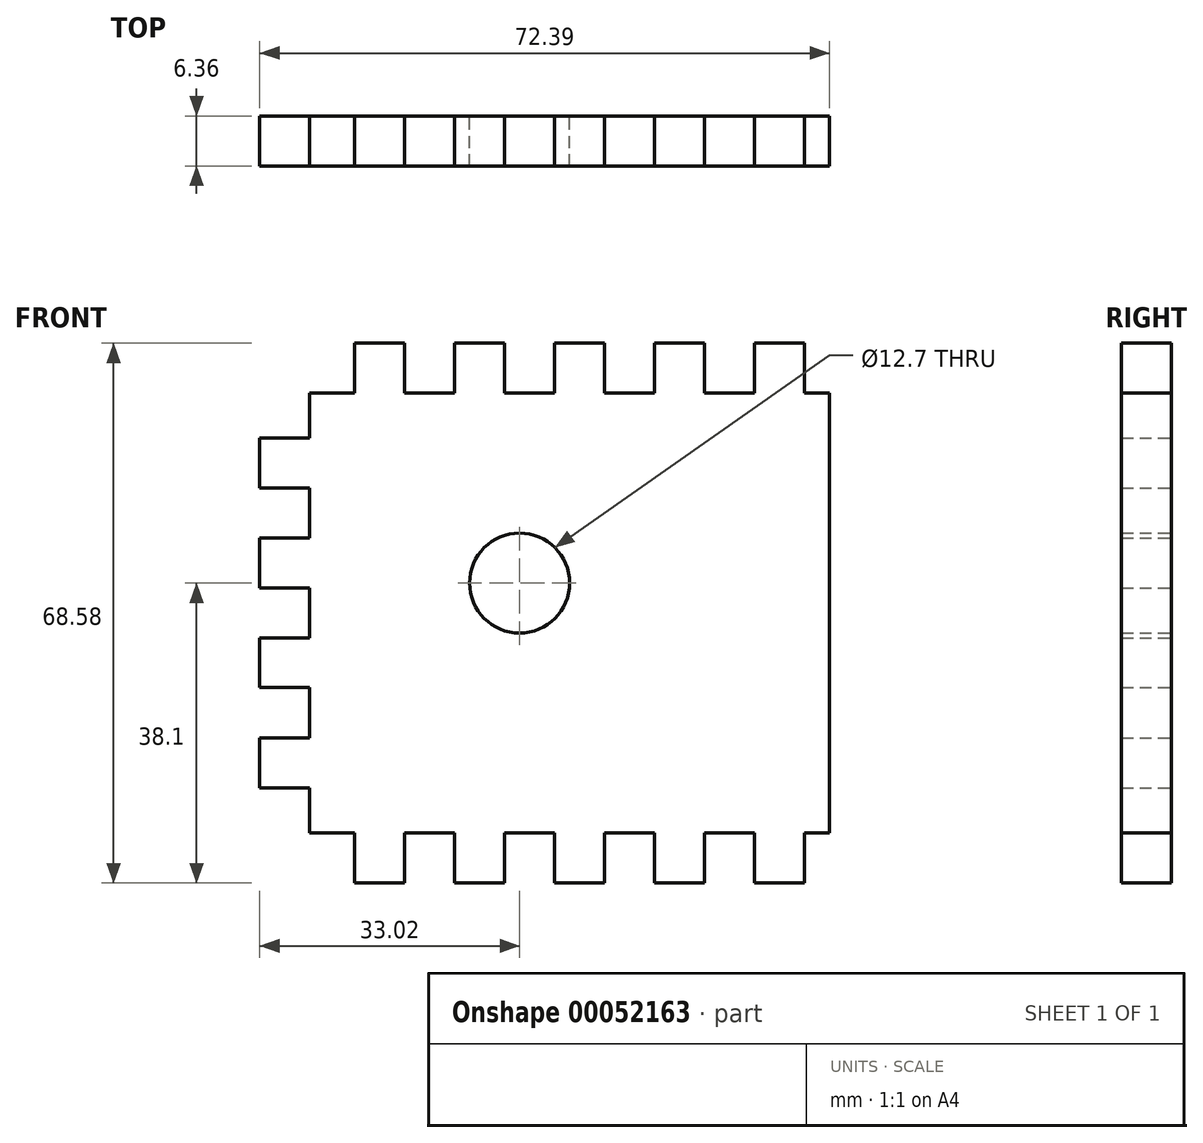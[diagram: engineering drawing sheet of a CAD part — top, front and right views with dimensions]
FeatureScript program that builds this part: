
annotation { "Feature Type Name" : "Feature", "Feature Type Description" : "" }
export const myFeature = defineFeature(function(context is Context, id is Id, definition is map)
    precondition{}
    {
        {
            var Q0;
            Q0=qCreatedBy(makeId("Front.planeOp"),FACE);
            var sketch = newSketch(context, id + "F0", { "sketchPlane" : qUnion([Q0])});
            skLineSegment(sketch, "E0.rect.bottom", {"start": v(33.02, 27.94) * mm, "end": v(29.85, 27.94) * mm});
            skLineSegment(sketch, "E0.rect.top", {"start": v(33.02, -27.94) * mm, "end": v(29.85, -27.94) * mm});
            skLineSegment(sketch, "E0.rect.left", {"start": v(33.02, 27.94) * mm, "end": v(33.02, -27.94) * mm});
            skPoint(sketch, "E0.rect.middle", {"position": v(0, 0) * mm});
            skLineSegment(sketch, "E1.top", {"start": v(23.5, 34.3) * mm, "end": v(29.85, 34.3) * mm});
            skLineSegment(sketch, "E1.left", {"start": v(23.5, 27.94) * mm, "end": v(23.5, 34.3) * mm});
            skLineSegment(sketch, "E1.right", {"start": v(29.85, 27.94) * mm, "end": v(29.85, 34.3) * mm});
            skLineSegment(sketch, "E2.1.0.1", {"start": v(10.8, 27.94) * mm, "end": v(10.8, 34.3) * mm});
            skLineSegment(sketch, "E2.1.0.2", {"start": v(10.8, 34.3) * mm, "end": v(17.15, 34.3) * mm});
            skLineSegment(sketch, "E2.1.0.3", {"start": v(17.15, 27.94) * mm, "end": v(17.15, 34.3) * mm});
            skLineSegment(sketch, "E2.2.0.1", {"start": v(-1.9, 27.94) * mm, "end": v(-1.9, 34.3) * mm});
            skLineSegment(sketch, "E2.2.0.2", {"start": v(-1.9, 34.3) * mm, "end": v(4.45, 34.3) * mm});
            skLineSegment(sketch, "E2.2.0.3", {"start": v(4.45, 27.94) * mm, "end": v(4.45, 34.3) * mm});
            skLineSegment(sketch, "E2.3.0.1", {"start": v(-14.6, 27.94) * mm, "end": v(-14.6, 34.3) * mm});
            skLineSegment(sketch, "E2.3.0.2", {"start": v(-14.6, 34.3) * mm, "end": v(-8.26, 34.3) * mm});
            skLineSegment(sketch, "E2.3.0.3", {"start": v(-8.26, 27.94) * mm, "end": v(-8.26, 34.3) * mm});
            skLineSegment(sketch, "E2.4.0.1", {"start": v(-27.3, 27.94) * mm, "end": v(-27.3, 34.3) * mm});
            skLineSegment(sketch, "E2.4.0.2", {"start": v(-27.3, 34.3) * mm, "end": v(-20.96, 34.3) * mm});
            skLineSegment(sketch, "E2.4.0.3", {"start": v(-20.96, 27.94) * mm, "end": v(-20.96, 34.3) * mm});
            skLineSegment(sketch, "E2.direction1", {"start": v(23.5, 27.94) * mm, "end": v(17.15, 27.94) * mm, "construction": true});
            skLineSegment(sketch, "E3.trimOffspring", {"start": v(-27.3, 27.94) * mm, "end": v(-33.02, 27.94) * mm});
            skLineSegment(sketch, "E4.trimOffspring", {"start": v(-14.6, 27.94) * mm, "end": v(-20.96, 27.94) * mm});
            skLineSegment(sketch, "E5.trimOffspring", {"start": v(10.8, 27.94) * mm, "end": v(4.45, 27.94) * mm});
            skLineSegment(sketch, "E6.trimOffspring", {"start": v(-1.9, 27.94) * mm, "end": v(-8.26, 27.94) * mm});
            skLineSegment(sketch, "E7.trimOffspring", {"start": v(23.5, 27.94) * mm, "end": v(17.15, 27.94) * mm});
            skLineSegment(sketch, "E8.MirrorCS", {"start": v(-27.3, -27.94) * mm, "end": v(-27.3, -34.3) * mm});
            skLineSegment(sketch, "E9.MirrorCS", {"start": v(10.8, -27.94) * mm, "end": v(10.8, -34.3) * mm});
            skLineSegment(sketch, "E10.MirrorCS", {"start": v(29.85, -27.94) * mm, "end": v(29.85, -34.3) * mm});
            skLineSegment(sketch, "E11.MirrorCS", {"start": v(-1.9, -27.94) * mm, "end": v(-1.9, -34.3) * mm});
            skLineSegment(sketch, "E12.MirrorCS", {"start": v(-1.9, -34.3) * mm, "end": v(4.45, -34.3) * mm});
            skLineSegment(sketch, "E13.MirrorCS", {"start": v(23.5, -34.3) * mm, "end": v(29.85, -34.3) * mm});
            skLineSegment(sketch, "E14.MirrorCS", {"start": v(17.15, -27.94) * mm, "end": v(17.15, -34.3) * mm});
            skLineSegment(sketch, "E15.MirrorCS", {"start": v(23.5, -27.94) * mm, "end": v(23.5, -34.3) * mm});
            skLineSegment(sketch, "E16.MirrorCS", {"start": v(-8.26, -27.94) * mm, "end": v(-8.26, -34.3) * mm});
            skLineSegment(sketch, "E17.MirrorCS", {"start": v(-27.3, -34.3) * mm, "end": v(-20.96, -34.3) * mm});
            skLineSegment(sketch, "E18.MirrorCS", {"start": v(-14.6, -34.3) * mm, "end": v(-8.26, -34.3) * mm});
            skLineSegment(sketch, "E19.MirrorCS", {"start": v(-14.6, -27.94) * mm, "end": v(-14.6, -34.3) * mm});
            skLineSegment(sketch, "E20.MirrorCS", {"start": v(10.8, -34.3) * mm, "end": v(17.15, -34.3) * mm});
            skLineSegment(sketch, "E21.MirrorCS", {"start": v(-20.96, -27.94) * mm, "end": v(-20.96, -34.3) * mm});
            skLineSegment(sketch, "E22.MirrorCS", {"start": v(4.44, -27.94) * mm, "end": v(4.44, -34.3) * mm});
            skLineSegment(sketch, "E23.trimOffspring", {"start": v(-27.3, -27.94) * mm, "end": v(-33.02, -27.94) * mm});
            skLineSegment(sketch, "E24.trimOffspring", {"start": v(-14.6, -27.94) * mm, "end": v(-20.96, -27.94) * mm});
            skLineSegment(sketch, "E25.trimOffspring", {"start": v(-1.9, -27.94) * mm, "end": v(-8.26, -27.94) * mm});
            skLineSegment(sketch, "E26.trimOffspring", {"start": v(10.8, -27.94) * mm, "end": v(4.45, -27.94) * mm});
            skLineSegment(sketch, "E27.trimOffspring", {"start": v(23.5, -27.94) * mm, "end": v(17.15, -27.94) * mm});
            skLineSegment(sketch, "E28", {"start": v(-33.02, 27.94) * mm, "end": v(-33.02, 22.23) * mm});
            skLineSegment(sketch, "E29.bottom", {"start": v(-33.02, 22.23) * mm, "end": v(-39.37, 22.23) * mm});
            skLineSegment(sketch, "E29.top", {"start": v(-33.02, 15.88) * mm, "end": v(-39.37, 15.88) * mm});
            skLineSegment(sketch, "E29.right", {"start": v(-39.37, 22.23) * mm, "end": v(-39.37, 15.88) * mm});
            skLineSegment(sketch, "E30.bottom", {"start": v(-33.02, 9.53) * mm, "end": v(-39.37, 9.53) * mm});
            skLineSegment(sketch, "E30.top", {"start": v(-33.02, 3.18) * mm, "end": v(-39.37, 3.18) * mm});
            skLineSegment(sketch, "E30.right", {"start": v(-39.37, 9.53) * mm, "end": v(-39.37, 3.18) * mm});
            skLineSegment(sketch, "E31.bottom", {"start": v(-33.02, -3.17) * mm, "end": v(-39.37, -3.17) * mm});
            skLineSegment(sketch, "E31.left", {"start": v(-33.02, -9.48) * mm, "end": v(-33.02, -9.52) * mm});
            skLineSegment(sketch, "E31.right", {"start": v(-39.37, -3.17) * mm, "end": v(-39.37, -9.52) * mm});
            skLineSegment(sketch, "E32.bottom", {"start": v(-33.02, -9.48) * mm, "end": v(-39.37, -9.48) * mm});
            skLineSegment(sketch, "E33.bottom", {"start": v(-33.02, -15.88) * mm, "end": v(-39.37, -15.88) * mm});
            skLineSegment(sketch, "E33.top", {"start": v(-33.02, -22.23) * mm, "end": v(-39.37, -22.23) * mm});
            skLineSegment(sketch, "E33.right", {"start": v(-39.37, -15.88) * mm, "end": v(-39.37, -22.23) * mm});
            skLineSegment(sketch, "E34.trimOffspring", {"start": v(-33.02, 15.88) * mm, "end": v(-33.02, 9.53) * mm});
            skLineSegment(sketch, "E35.trimOffspring", {"start": v(-33.02, 3.18) * mm, "end": v(-33.02, -3.17) * mm});
            skLineSegment(sketch, "E36.trimOffspring", {"start": v(-33.02, -9.48) * mm, "end": v(-33.02, -15.88) * mm});
            skLineSegment(sketch, "E37.trimOffspring", {"start": v(-33.02, -22.23) * mm, "end": v(-33.02, -27.94) * mm});
            skCircle(sketch, "E38", {"center": v(-6.35, 3.81) * mm, "radius": 6.35 * mm});
            skSolve(sketch);
        }
        {
            var Q0;
            Q0=makeQuery(id+"F0.imprint","IMPRINT",FACE,{"disambiguationData":[TD([[makeQuery(id+"F0.imprint","IMPRINT",EDGE,{"derivedFrom":sQuery(id+"F0.wireOp",EDGE,"E0.rect.bottom")}),1.0]])]});
            extrude(context, id + "F1", {"entities" : qUnion([Q0]), "endBound" : BoundingType.SYMMETRIC, "depth" : 6.35 * mm});
        }
    });
